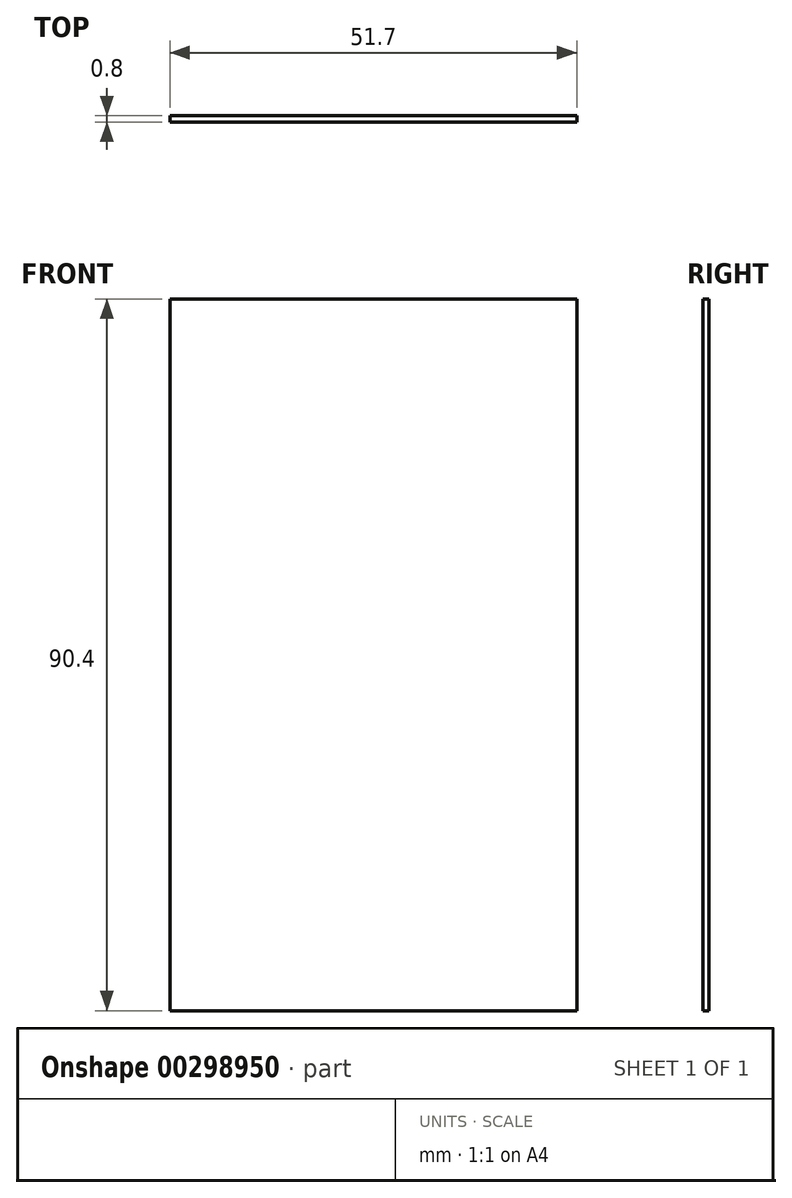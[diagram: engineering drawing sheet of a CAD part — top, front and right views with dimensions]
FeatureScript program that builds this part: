
annotation { "Feature Type Name" : "Feature", "Feature Type Description" : "" }
export const myFeature = defineFeature(function(context is Context, id is Id, definition is map)
    precondition{}
    {
        {
            var Q0;
            Q0=qCreatedBy(makeId("Front.planeOp"),FACE);
            var sketch = newSketch(context, id + "F0", { "sketchPlane" : qUnion([Q0])});
            skLineSegment(sketch, "E0.bottom", {"start": v(25.85, -45.2) * mm, "end": v(-25.85, -45.2) * mm});
            skLineSegment(sketch, "E0.top", {"start": v(25.85, 45.2) * mm, "end": v(-25.85, 45.2) * mm});
            skLineSegment(sketch, "E0.left", {"start": v(25.85, -45.2) * mm, "end": v(25.85, 45.2) * mm});
            skLineSegment(sketch, "E0.right", {"start": v(-25.85, -45.2) * mm, "end": v(-25.85, 45.2) * mm});
            skPoint(sketch, "E0.middle", {"position": v(0, 0) * mm});
            skSolve(sketch);
        }
        {
            var Q0;
            Q0=makeQuery(id+"F0.imprint","IMPRINT",FACE,{"disambiguationData":[TD([[makeQuery(id+"F0.imprint","IMPRINT",EDGE,{"derivedFrom":sQuery(id+"F0.wireOp",EDGE,"E0.bottom")}),-1.0]])]});
            extrude(context, id + "F1", {"entities" : qUnion([Q0]), "depth" : .8 * mm});
        }
    });
